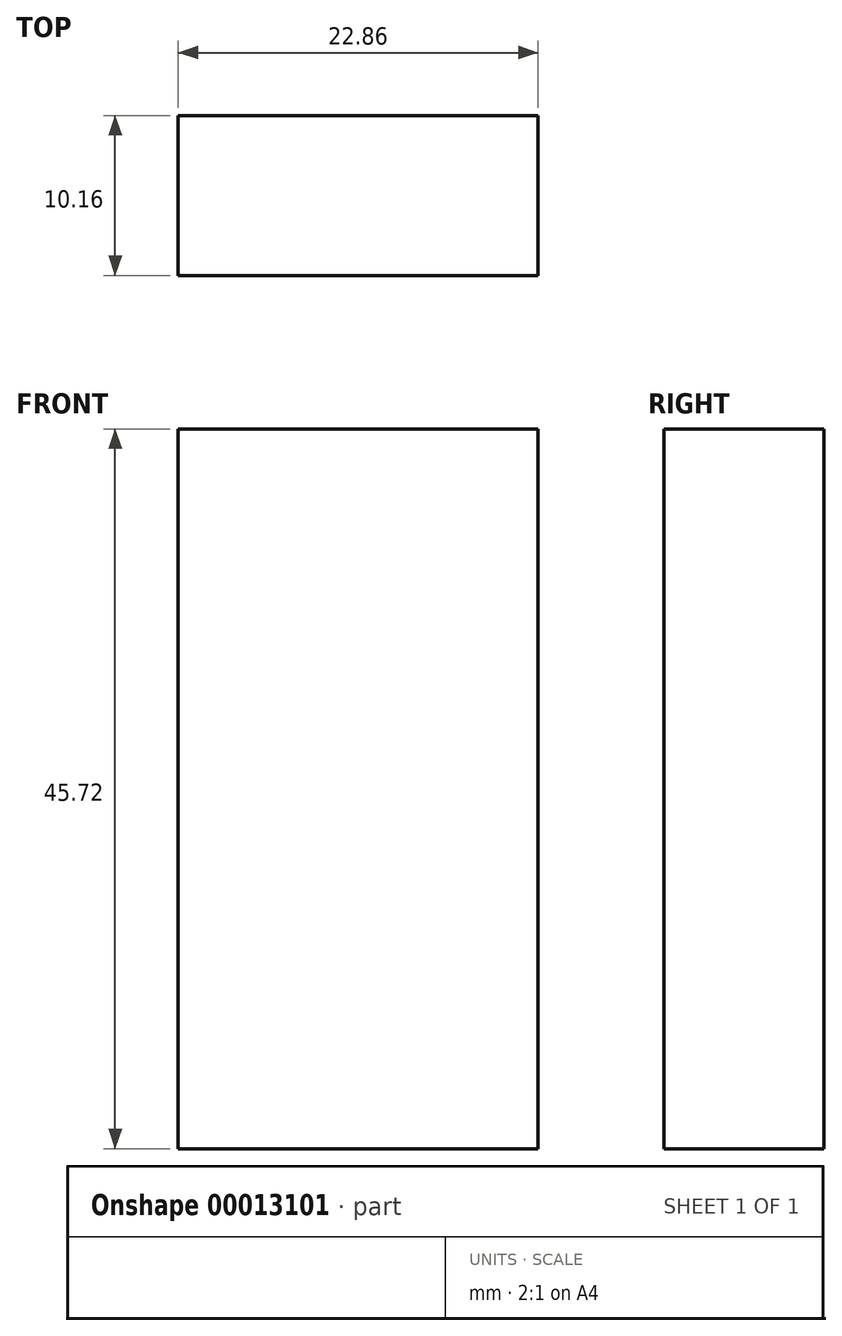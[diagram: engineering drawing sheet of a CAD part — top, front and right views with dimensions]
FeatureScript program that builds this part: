
annotation { "Feature Type Name" : "Feature", "Feature Type Description" : "" }
export const myFeature = defineFeature(function(context is Context, id is Id, definition is map)
    precondition{}
    {
        {
            var Q0;
            Q0=qCreatedBy(makeId("Front.planeOp"),FACE);
            var sketch = newSketch(context, id + "F0", { "sketchPlane" : qUnion([Q0])});
            skLineSegment(sketch, "E0.bottom", {"start": v(18.3, 20.37) * mm, "end": v(41.15, 20.37) * mm});
            skLineSegment(sketch, "E0.top", {"start": v(18.3, -25.35) * mm, "end": v(41.15, -25.35) * mm});
            skLineSegment(sketch, "E0.left", {"start": v(18.3, 20.37) * mm, "end": v(18.3, -25.35) * mm});
            skLineSegment(sketch, "E0.right", {"start": v(41.15, 20.37) * mm, "end": v(41.15, -25.35) * mm});
            skSolve(sketch);
        }
        {
            var Q0;
            Q0=makeQuery(id+"F0.imprint","IMPRINT",FACE,{"disambiguationData":[TD([[makeQuery(id+"F0.imprint","IMPRINT",EDGE,{"derivedFrom":sQuery(id+"F0.wireOp",EDGE,"E0.bottom")}),-1.0]])]});
            extrude(context, id + "F1", {"entities" : qUnion([Q0]), "depth" : 10.16 * mm, "offsetDistance" : 25.4 * mm});
        }
    });
